# Revit family: PARETE_01
name_source: partatom
category: Осветительные приборы
revit_build: Autodesk Revit 2016 (Build: 20150220_1215(x64)
units: mm (PartAtom-declared; Revit-internal decimal feet)

## family parameters
Всегда вертикально = Нет
Заголовок OmniClass = Lighting
Источник света = Да
На основе рабочей плоскости = Да
Номер OmniClass = 23.80.70.00
Общий = Нет
При загрузке вырезать с полостями = Нет
Размер круглого соединителя = Использовать диаметр
Тип детали = Нормальный
Точка расчета площади = Нет

## types (4) — shared parameters
ADSK_Единица измерения = Шт.
ADSK_Завод-изготовитель = ООО МГК Световые технологии
ADSK_Количество фаз числовое = 1
ADSK_Коэффициент мощности = 0.96
ADSK_Наименование = Семейство настенных светильников, создающих диффузное освещение. Рассеиватель из выдувного трехслойного опалового стекла ручной работы. Корпус изготовлен из хромированного металла
ADSK_Напряжение = 230 В
ADSK_Номинальная мощность = 0 кВ·А
ADSK_Полная мощность = 0 кВт
ADSK_Размер_Высота = 495 мм
ADSK_Размер_Длина = 96 мм
ADSK_Размер_Радиус = 33 мм
ADSK_Размер_Ширина = 66 мм
ADSK_Ток = 0 А
ADSK_Энергоэффективность = 0 лм/Вт
IP Class = IP44
URL = http://ltcompany.com
Блок аварийного питания = Нет
Видимая форма излучения при визуализации = Нет
Группа модели = Светильники
Изготовитель = ООО МГК Световые технологии
Излучение по длине прямоугольника = 66 мм
Излучение по ширине прямоугольника = 66 мм
Класс Защиты = I
Класс пожароопасности = Нет
Климатическая зона = УХЛ4
Код по классификатору = D5020200
Корпус = Корпус белый металл
Область использования = Гостиницы Индивидуальные дома Культурно-развлекательные Магазины Бутики Объекты бытового обслуживания Объекты общественного питания Офисы ТРЦ
Описание = Семейство настенных светильников, создающих диффузное освещение. Рассеиватель из выдувного трехслойного опалового стекла ручной работы. Корпус изготовлен из хромированного металла
Переменная.цоколь = 80 мм
Плафон = Плафон белый полупрозрачный
Плафон.длина = 350 мм
Полная установленная мощность = 0 кВт
Разработчик = ООО ПРОРУБИМ
Разработчик (телефон) = +7 (495) 649-85-43
Свет.положение = 175 мм
Светофильтр = 16777215
Смещение цветовой температуры при затухании лампы = <Нет>
Угол наклона = 60.00°
zero-valued in all types: ADSK_Масса, Отметка по умолчанию

## per-type parameters (varying)
| type | Плафон 2 | Плафон нижний | Файл фотометрической сетки |
| PARETE 1 | 178 мм | Нет | Parete.IES |
| PARETE GRANDE | 330 мм | Нет | Parete Grande.IES |
| PARETE GRANDE LED 3000K | 330 мм | Нет | Parete Grande.IES |
| PARETE 2 | 178 мм | Да | Parete 2.IES |
